AUTODESK INVENTOR PART (.ipt)
format: ipt  version: 2014 SP1 (Build 180222100, 222)  size: 93,184 bytes
history: native  units: in
note: dims shown in document units (in); Inventor stores cm internally (conversion verified against a paired STEP export)
features: sketch x4, extrude x2, plane x2
ambient origin geometry x8: Origin, YZ Plane, XZ Plane, XY Plane, X Axis, Y Axis, Z Axis, Center Point
bodies: Solid1 (feature_tree)
feature tree (8):
  extrude  "Extrusion1"  Depth=310.0in TaperAngle=0.0deg
  sketch  "Sketch2"  dims[d11=0.15in d12=0.0206in]
  plane  "Work Plane1"
  sketch  "Sketch5"  dims[d13=0.3in]
  plane  "Work Plane2"
  extrude  "Extrusion4"  Depth=0.15in
  sketch  "Sketch1"  dims[d0=0.3in d2=310.0in d3=0.0in]
  sketch  "Sketch6"  dims[d14=177.0in d15=0.0in]
